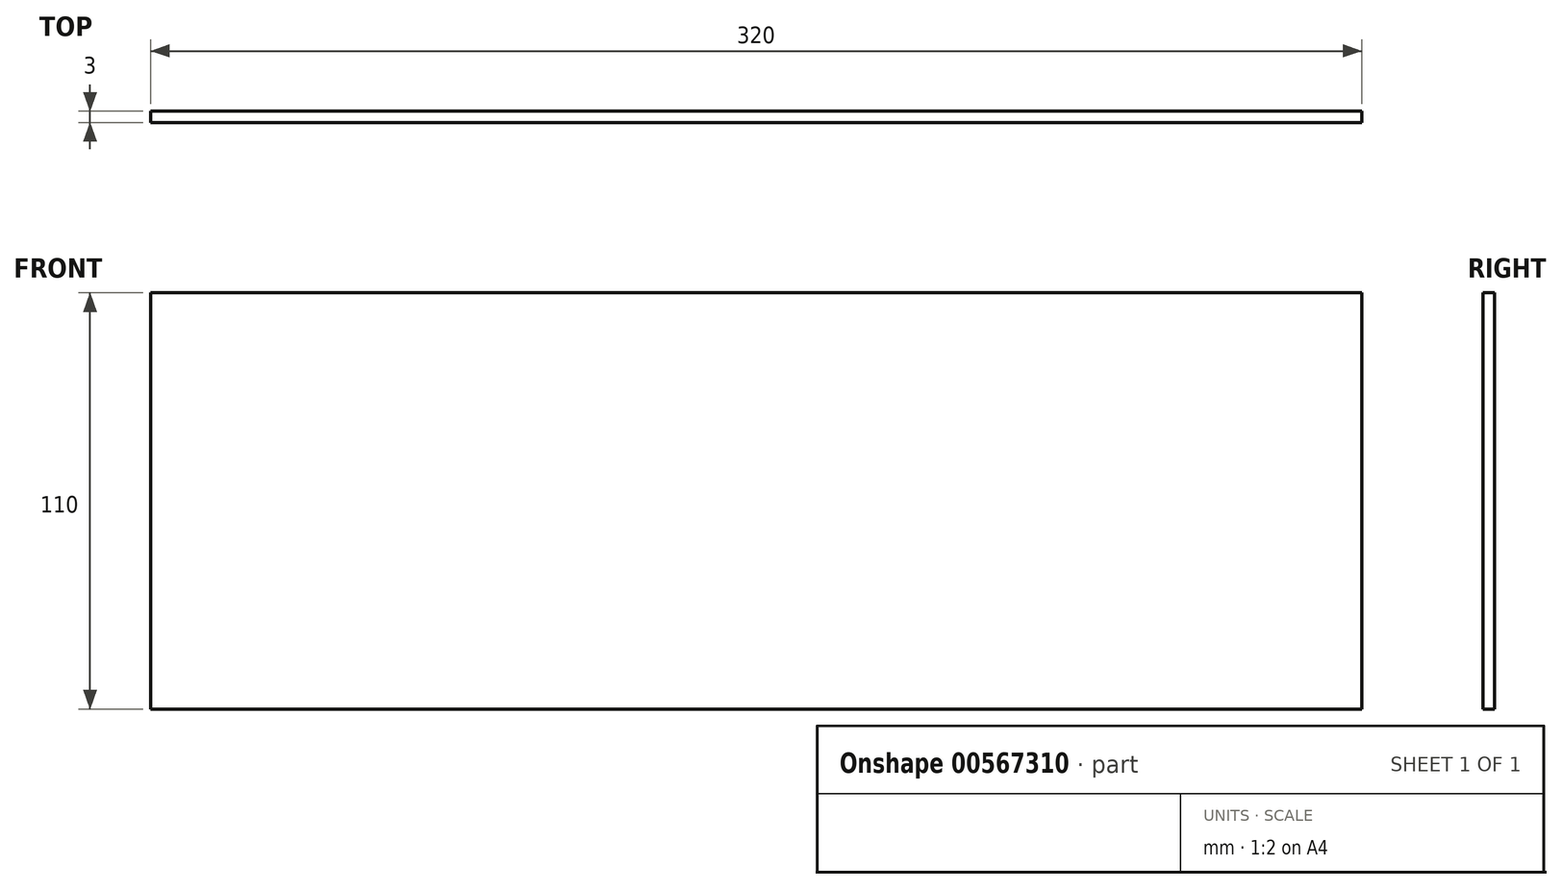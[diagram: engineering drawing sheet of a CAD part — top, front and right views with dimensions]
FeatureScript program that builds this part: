
annotation { "Feature Type Name" : "Feature", "Feature Type Description" : "" }
export const myFeature = defineFeature(function(context is Context, id is Id, definition is map)
    precondition{}
    {
        {
            var Q0;
            Q0=qCreatedBy(makeId("Front.planeOp"),FACE);
            var sketch = newSketch(context, id + "F0", { "sketchPlane" : qUnion([Q0])});
            skLineSegment(sketch, "E0.bottom", {"start": v(160, 55) * mm, "end": v(-160, 55) * mm});
            skLineSegment(sketch, "E0.top", {"start": v(160, -55) * mm, "end": v(-160, -55) * mm});
            skLineSegment(sketch, "E0.left", {"start": v(160, 55) * mm, "end": v(160, -55) * mm});
            skLineSegment(sketch, "E0.right", {"start": v(-160, 55) * mm, "end": v(-160, -55) * mm});
            skPoint(sketch, "E0.middle", {"position": v(0, 0) * mm});
            skSolve(sketch);
        }
        {
            var Q0;
            Q0=makeQuery(id+"F0.imprint","IMPRINT",FACE,{"disambiguationData":[TD([[makeQuery(id+"F0.imprint","IMPRINT",EDGE,{"derivedFrom":sQuery(id+"F0.wireOp",EDGE,"E0.bottom")}),1.0]])]});
            extrude(context, id + "F1", {"entities" : qUnion([Q0]), "depth" : 3 * mm, "offsetDistance" : 25 * mm});
        }
        {
            var Q0;
            Q0=makeQuery(id+"F1.opExtrude","SWEPT_FACE",FACE,{"disambiguationData":[OSD([sQuery(id+"F0.wireOp",EDGE,"E0.bottom")])]});
            var sketch = newSketch(context, id + "F2", { "sketchPlane" : qUnion([Q0])});
            skLineSegment(sketch, "E1", {"start": v(0, 0) * mm, "end": v(0, -3) * mm});
            skPoint(sketch, "E2", {"position": v(0, -1.5) * mm});
            skSolve(sketch);
        }
    });
